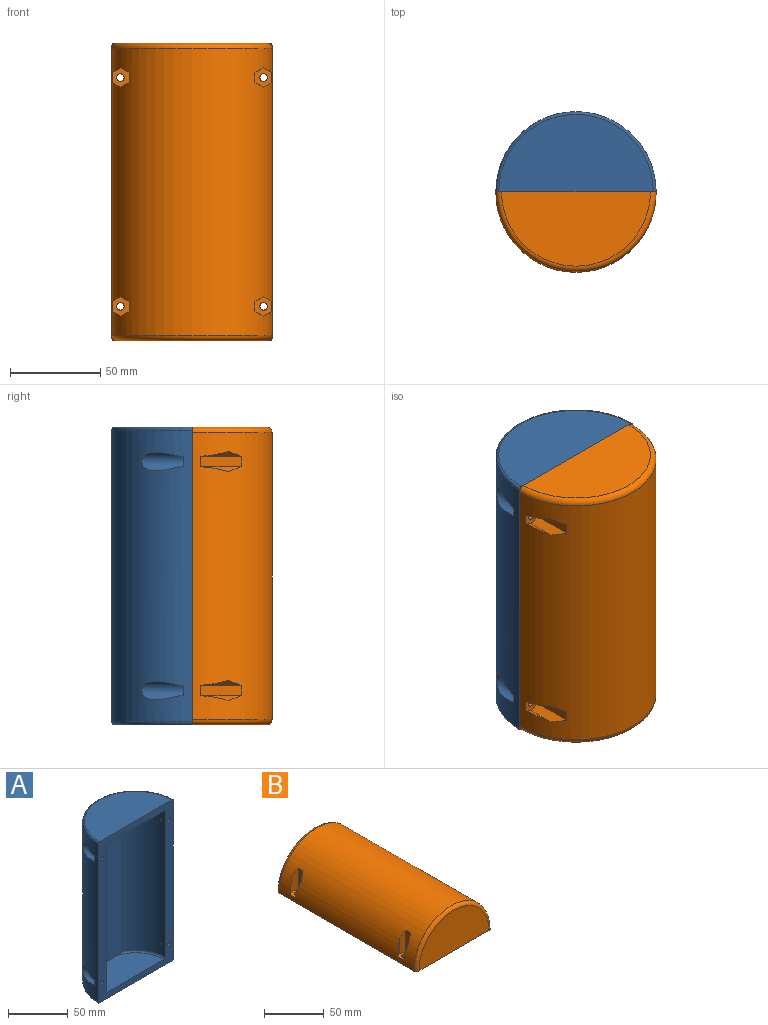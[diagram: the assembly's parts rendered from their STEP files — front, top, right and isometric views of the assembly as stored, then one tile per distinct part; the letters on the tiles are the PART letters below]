
ASSEMBLY  parts=2 mates=1
PART A: 25 faces, bbox 96.2x48.1x165.1 mm
  f0: cylinder r=44.45mm len=161.93mm, axis (0,0,-1), area 21793.5mm2, adj f1,f13,f14,f15,f16,f17,f18,f19
  f1: plane 165.1x88.9mm, normal (0,-1,0), area 3976mm2, adj f0,f2,f4,f5,f6,f7,f8,f9
  f2: cylinder r=34.92mm len=150.81mm, axis (0,0,-1), area 6010.3mm2, adj f1,f3,f5,f24
  f3: plane 152.4x29.1mm, normal (0,-1,0), area 4432mm2, adj f2,f4,f5,f7,f23,f24
  f4: cylinder r=34.92mm len=150.81mm, axis (0,0,-1), area 6010.3mm2, adj f1,f3,f7,f23
  f5: plane 68.26x31.75mm, normal (0,0,1), area 1789mm2, adj f1,f2,f3,f23
  f6: plane 85.73x42.86mm, normal (0,0,-1), area 2885.9mm2, adj f1,f22
  f7: plane 68.26x31.75mm, normal (0,0,-1), area 1789mm2, adj f1,f3,f4,f24
  f8: plane 85.73x42.86mm, normal (0,0,1), area 2885.9mm2, adj f1,f21
  f9: cylinder r=2.1mm len=4.76mm, axis (0,-1,0), area 62.7mm2, adj f1,f20
  f10: cylinder r=2.1mm len=4.76mm, axis (0,-1,0), area 62.7mm2, adj f1,f18
  f11: cylinder r=2.1mm len=4.76mm, axis (0,-1,0), area 62.7mm2, adj f1,f16
  f12: cylinder r=2.1mm len=4.76mm, axis (0,-1,0), area 62.7mm2, adj f1,f14
  f13: cylinder r=5.08mm len=23.14mm, axis (0,-1,0), area 421mm2, adj f0,f14
  f14: plane 10.16x9.59mm, normal (0,1,0), area 65.5mm2, adj f0,f12,f13
  f15: cylinder r=5.08mm len=23.14mm, axis (0,-1,0), area 421mm2, adj f0,f16
  f16: plane 10.16x9.59mm, normal (0,1,0), area 65.5mm2, adj f0,f11,f15
  f17: cylinder r=5.08mm len=23.14mm, axis (0,-1,0), area 421.4mm2, adj f0,f18
  f18: plane 10.16x9.59mm, normal (0,1,0), area 65.5mm2, adj f0,f10,f17
  f19: cylinder r=5.08mm len=23.14mm, axis (0,-1,0), area 421.4mm2, adj f0,f20
  f20: plane 10.16x9.59mm, normal (0,1,0), area 65.5mm2, adj f0,f9,f19
  f21: torus R=42.86mm, axis (0,0,1), area 343.7mm2, adj f0,f1,f8
  f22: torus R=42.86mm, axis (0,0,-1), area 343.7mm2, adj f0,f1,f6
  f23: torus R=33.34mm, axis (0,0,-1), area 101.1mm2, adj f1,f3,f4,f5
  f24: torus R=33.34mm, axis (0,0,1), area 101.1mm2, adj f1,f2,f3,f7
PART B: 53 faces, bbox 96.3x165.1x50.7 mm
  f0: cylinder r=44.45mm len=158.75mm, axis (0,1,0), area 21367mm2, adj f5,f17,f18,f19,f20,f21,f22,f23
  f1: cylinder r=2.1mm len=4.76mm, axis (0,0,-1), area 62.7mm2, adj f5,f40
  f2: cylinder r=2.1mm len=4.76mm, axis (0,0,-1), area 62.7mm2, adj f5,f34
  f3: cylinder r=2.1mm len=4.76mm, axis (0,0,-1), area 62.7mm2, adj f5,f28
  f4: cylinder r=2.1mm len=4.76mm, axis (0,0,-1), area 62.7mm2, adj f5,f22
  f5: plane 165.15x88.95mm, normal (0,0,-1), area 2788.4mm2, adj f0,f1,f2,f3,f4,f6,f7,f9
  f6: cylinder r=39.69mm len=146.05mm, axis (0,1,0), area 4667.2mm2, adj f5,f8,f42,f44,f48,f51
  f7: cylinder r=39.69mm len=146.05mm, axis (0,1,0), area 4667.3mm2, adj f5,f8,f41,f43,f47,f50
  f8: plane 146.05x47.63mm, normal (0,0,-1), area 6955.6mm2, adj f6,f7,f49,f52
  f9: plane 73.03x28.58mm, normal (0,1,0), area 1847.8mm2, adj f5,f50,f51,f52
  f10: plane 82.55x41.28mm, normal (0,-1,0), area 2676mm2, adj f5,f46
  f11: plane 73.03x28.58mm, normal (0,-1,0), area 1847.8mm2, adj f5,f47,f48,f49
  f12: plane 82.55x41.28mm, normal (0,1,0), area 2676mm2, adj f5,f45
  f13: cylinder r=6.35mm len=20.58mm, axis (0,0,-1), area 251.5mm2, adj f5,f44
  f14: cylinder r=6.35mm len=20.58mm, axis (0,0,-1), area 251.4mm2, adj f5,f43
  f15: cylinder r=6.35mm len=20.58mm, axis (0,0,-1), area 251.4mm2, adj f5,f42
  f16: cylinder r=6.35mm len=20.58mm, axis (0,0,-1), area 251.5mm2, adj f5,f41
  f17: plane 15.26x4.51mm, normal (0.5,0.87,0), area 48.5mm2, adj f0,f18,f22
  f18: plane 22.73x4.76mm, normal (-0.5,0.87,0), area 106mm2, adj f0,f17,f19,f22
  f19: plane 22.73x5.5mm, normal (-1,0,0), area 125mm2, adj f0,f18,f20,f22
  f20: plane 22.73x4.76mm, normal (-0.5,-0.87,0), area 106mm2, adj f0,f19,f21,f22
  f21: plane 15.26x4.51mm, normal (0.5,-0.87,0), area 48.5mm2, adj f0,f20,f22
  f22: plane 11x9.27mm, normal (0,0,1), area 63.3mm2, adj f0,f4,f17,f18,f19,f20,f21
  f23: plane 15.26x4.51mm, normal (-0.5,-0.87,0), area 48.5mm2, adj f0,f24,f28
  f24: plane 22.73x4.76mm, normal (0.5,-0.87,0), area 106mm2, adj f0,f23,f25,f28
  f25: plane 22.73x5.5mm, normal (1,0,0), area 125mm2, adj f0,f24,f26,f28
  f26: plane 22.73x4.76mm, normal (0.5,0.87,0), area 106mm2, adj f0,f25,f27,f28
  f27: plane 15.26x4.51mm, normal (-0.5,0.87,0), area 48.5mm2, adj f0,f26,f28
  f28: plane 11x9.27mm, normal (0,0,1), area 63.3mm2, adj f0,f3,f23,f24,f25,f26,f27
  f29: plane 22.73x4.76mm, normal (0.5,-0.87,0), area 106mm2, adj f0,f30,f33,f34
  f30: plane 22.73x5.5mm, normal (1,0,0), area 125mm2, adj f0,f29,f31,f34
  f31: plane 22.73x4.76mm, normal (0.5,0.87,0), area 106mm2, adj f0,f30,f32,f34
  f32: plane 15.26x4.51mm, normal (-0.5,0.87,0), area 48.5mm2, adj f0,f31,f34
  f33: plane 15.26x4.51mm, normal (-0.5,-0.87,0), area 48.5mm2, adj f0,f29,f34
  f34: plane 11x9.27mm, normal (0,0,1), area 63.3mm2, adj f0,f2,f29,f30,f31,f32,f33
  f35: plane 22.73x4.76mm, normal (-0.5,0.87,0), area 106mm2, adj f0,f36,f39,f40
  f36: plane 22.73x5.5mm, normal (-1,0,0), area 125mm2, adj f0,f35,f37,f40
  f37: plane 22.73x4.76mm, normal (-0.5,-0.87,0), area 106mm2, adj f0,f36,f38,f40
  f38: plane 15.26x4.51mm, normal (0.5,-0.87,0), area 48.5mm2, adj f0,f37,f40
  f39: plane 15.26x4.51mm, normal (0.5,0.87,0), area 48.5mm2, adj f0,f35,f40
  f40: plane 11x9.27mm, normal (0,0,1), area 63.3mm2, adj f0,f1,f35,f36,f37,f38,f39
  f41: bspline ~24.94x17.97mm, area 158.3mm2, adj f5,f7,f16
  f42: bspline ~24.94x17.97mm, area 158.2mm2, adj f5,f6,f15
  f43: bspline ~24.94x17.97mm, area 158.2mm2, adj f5,f7,f14
  f44: bspline ~24.94x17.97mm, area 158.3mm2, adj f5,f6,f13
  f45: torus R=41.27mm, axis (0,1,0), area 678.4mm2, adj f0,f5,f12
  f46: torus R=41.27mm, axis (0,-1,0), area 678.4mm2, adj f0,f5,f10
  f47: torus R=36.51mm, axis (0,1,0), area 176.3mm2, adj f5,f7,f11,f49
  f48: torus R=36.51mm, axis (0,1,0), area 176.3mm2, adj f5,f6,f11,f49
  f49: cylinder r=3.17mm len=47.63mm, axis (-1,0,0), area 233.6mm2, adj f8,f11,f47,f48
  f50: torus R=36.51mm, axis (0,-1,0), area 176.3mm2, adj f5,f7,f9,f52
  f51: torus R=36.51mm, axis (0,-1,0), area 176.3mm2, adj f5,f6,f9,f52
  f52: cylinder r=3.17mm len=47.63mm, axis (-1,0,0), area 233.6mm2, adj f8,f9,f50,f51
PLACE A at identity fixed
PLACE B rot(axis=(1,0,0),90deg) t=(0,0,152.4)mm
MATE fastened A.f12 <-> B.f1  axis (0,-1,0) through (-39.69,0,139.7)mm
